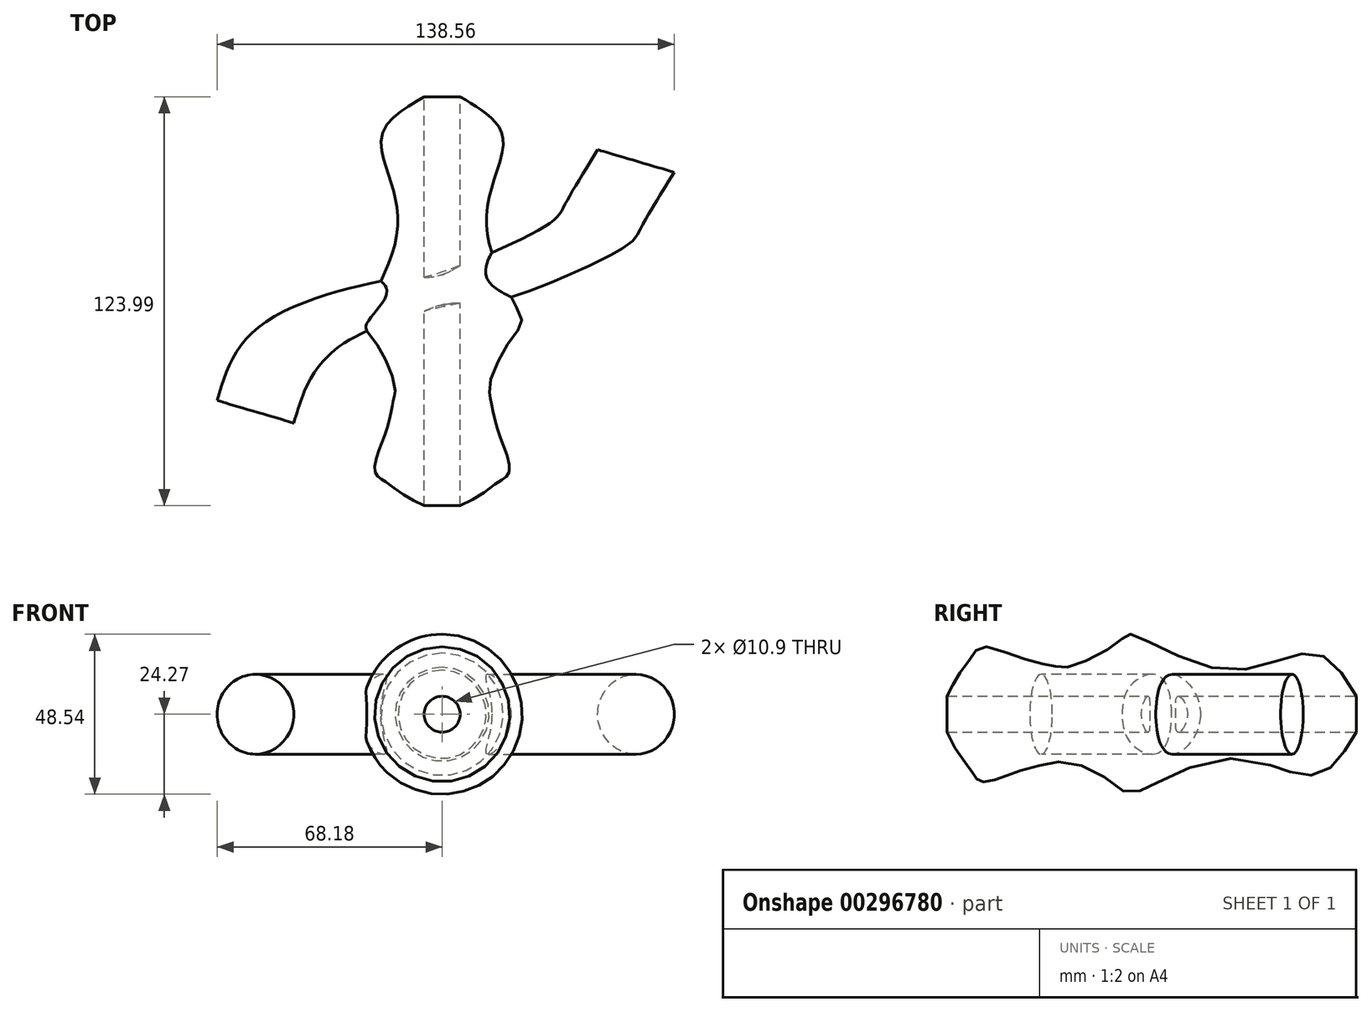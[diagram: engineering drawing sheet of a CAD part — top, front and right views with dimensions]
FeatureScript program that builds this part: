
annotation { "Feature Type Name" : "Feature", "Feature Type Description" : "" }
export const myFeature = defineFeature(function(context is Context, id is Id, definition is map)
    precondition{}
    {
        {
            var Q0;
            Q0=qCreatedBy(makeId("Top.planeOp"),FACE);
            var sketch = newSketch(context, id + "F0", { "sketchPlane" : qUnion([Q0])});
            skFitSpline(sketch, "E0", {"points": [v(0, 61.3) * mm, v(18.14, 46.78) * mm, v(13.4, 19.06) * mm, v(24.25, -10.5) * mm, v(22.34, -13.56) * mm, v(14.51, -28.64) * mm, v(14.7, -33.8) * mm, v(16.8, -42.96) * mm, v(20.43, -55.57) * mm, v(17.38, -58.62) * mm, v(11.27, -63.02) * mm, v(5.73, -65.88) * mm, v(0, -69.7) * mm], "startDerivative": vector(159.65, -108.9) * mm, "endDerivative": vector(-88.79, -64.5) * mm});
            skLineSegment(sketch, "E1", {"start": v(0, 61.3) * mm, "end": v(0, -69.7) * mm});
            skSolve(sketch);
        }
        {
            var Q0;
            Q0 = qSketchRegion(id + "F0", true);
            var Q1;
            Q1=sQuery(id+"F0.wireOp",EDGE,"E1");
            revolve(context, id + "F1", {"entities" : qUnion([Q0]), "axis" : qUnion([Q1]), "revolveType" : RevolveType.FULL});
        }
        {
            var Q0;
            Q0=qCreatedBy(makeId("Front.planeOp"),FACE);
            var sketch = newSketch(context, id + "F2", { "sketchPlane" : qUnion([Q0])});
            skCircle(sketch, "E2", {"center": v(0, 0) * mm, "radius": 5.45 * mm});
            skSolve(sketch);
        }
        {
            var Q0;
            Q0 = qSketchRegion(id + "F2", true);
            extrude(context, id + "F3", {"entities" : qUnion([Q0]), "operationType" : NewBodyOperationType.REMOVE, "endBound" : BoundingType.THROUGH_ALL, "depth" : 25.4 * mm, "hasSecondDirection" : true, "secondDirectionBound" : SecondDirectionBoundingType.THROUGH_ALL, "secondDirectionOppositeDirection" : true, "secondDirectionDepth" : 25.4 * mm});
        }
        {
            var Q0;
            Q0=qCreatedBy(makeId("Top.planeOp"),FACE);
            var sketch = newSketch(context, id + "F4", { "sketchPlane" : qUnion([Q0])});
            skFitSpline(sketch, "E3", {"points": [v(-56.7, -37.53) * mm, v(-41.1, -13.08) * mm, v(3.3, 0) * mm, v(6.75, 0) * mm, v(43.2, 15.57) * mm, v(48.75, 22.02) * mm, v(58.65, 38.52) * mm], "startDerivative": vector(40.43, 137.26) * mm, "endDerivative": vector(74.4, 119.37) * mm});
            skSolve(sketch);
        }
        {
            var Q0;
            Q0=sQuery(id+"F4.wireOp",VERTEX,"E3.0.internal");
            var Q1;
            Q1=sQuery(id+"F4.wireOp",EDGE,"E3");
            cPlane(context, id + "F5", {"entities" : qUnion([Q0, Q1]), "cplaneType" : CPlaneType.CURVE_POINT, "offset" : 25.4 * mm, "width" : 152.4 * mm, "height" : 152.4 * mm});
        }
        {
            var Q0;
            Q0=qCreatedBy(id+"F5.planeOp",FACE);
            var sketch = newSketch(context, id + "F6", { "sketchPlane" : qUnion([Q0])});
            skCircle(sketch, "E4", {"center": v(43.65, 0) * mm, "radius": 12.1 * mm});
            skSolve(sketch);
        }
        {
            var Q0;
            Q0=makeQuery(id+"F6.imprint","IMPRINT",FACE,{"disambiguationData":[TD([[makeQuery(id+"F6.imprint","IMPRINT",EDGE,{"derivedFrom":sQuery(id+"F6.wireOp",EDGE,"E4")}),1.0]])]});
            var Q1;
            Q1=sQuery(id+"F4.wireOp",EDGE,"E3");
            sweep(context, id + "F7", {"operationType" : NewBodyOperationType.ADD, "profiles" : qUnion([Q0]), "path" : qUnion([Q1]), "keepProfileOrientation" : true});
        }
    });
